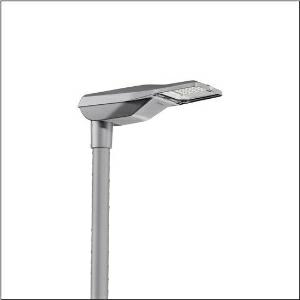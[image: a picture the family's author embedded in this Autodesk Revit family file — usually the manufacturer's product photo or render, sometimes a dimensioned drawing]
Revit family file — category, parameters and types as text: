
# Revit family: streetlight_sl_21_iq_micro___st1_5a_5xe1p31d08cb_2d79
name_source: partatom
category: Lighting Fixtures
units: mm (PartAtom-declared; Revit-internal decimal feet)

## family parameters
Cut with Voids When Loaded = No
Host = Face
Light Source = No
Part Type = Normal
Room Calculation Point = No
Round Connector Dimension = Use Diameter
Shared = No

## types (1)
- --- (1 x LED, 2820 lm, 19.4 W, 3000K)
    Apparent Load = 19 VA
    CIE Flux Codes = 22 53 95 100 100
    Color Rendering = 70
    Color Temperature = 3000K
    Default Elevation = 1800 mm
    Description = Streetlight SL 21 iQ micro, mast luminaire, primary light control with lens, of PMMA, primary optical cover: cover, of toughened safety glass, transparent, light distribution: ST1.5a, light emission: direct distribution, primary light characteristic: asymmetric, installation type: post-top, side-entry, LED, High Power LED, rated luminous flux: 2.820lm, luminous efficacy: 145lm/W, light colour: 730, colour temperature: 3000K, control gear: iQ-Comfort, control: Auto-Match, Temp-Guard, Lumen-Switch, Night-Set, Smart-Wire, Light-Fading, Desk-Remote (wireless, voltage-free reading and setting of iQ features in the workshop via application-optimized NFC function/RFID function), optimised constant luminous flux control (CLO 2.0), pre-setting: linear dimming characteristic, mains connection: 220..240V, AC, 50/60Hz, start of lifetime: 19W, end of service life: 20W, reduction: 10W, luminaire housing, of diecast aluminium, powder-coated, Siteco® metallic grey (DB 702S), corrosivity category C5 mid according to DIN EN ISO 12944, please order mast flange separately, inclination adjustable: 0°, 5°, 10°, 15°, sealing non-destructively replaceable, multi-level sealing system, length: 528mm, width: 235mm, height: 110mm, mast flange for spigot size: 42mm (side-entry): 5XC10008XM4, 60/48mm (side-entry/post-top): 5XC10108XM2, 76/60mm (side-entry/post-top): 5XC10108XM1, protection rating (complete): IP66, insulation class (complete): insulation class II (safety insulation), certification: CE, ENEC, ENEC+, VDE, impact resistance: IK10, permissible operating ambient temperature for outdoor applications: -40..+50°C, standard-compliant lighting for roads and squares, packaging unit: 1 piece

Light Distribution: ST1.5a
    Height = 110 mm
    Lamp = 1 x LED
    Lamp Light Flux = 2820 lm
    Lamp Power = 19.4 W
    Lamp count = 1
    Length = 528 mm
    Luminous efficacy = 145 lm/W
    Manufacturer = Siteco
    ModVariant = No
    Model = 5XE1P31D08CB
    Number of Poles = 1
    OnlyDefault = Yes
    Power Factor = 1
    Product Name = Streetlight SL 21 iQ micro | ST1.5a
    Product group = mast luminaire | pylon top
    ProductGroupID = 6100
    Protection Class = Protection class II
    Protection Degree = IP 66
    RLX_Detail_Level = 1
    RLX_Emergency_Light_Flux = 0 lm
    RLX_Emergency_Type = 0
    RLX_Emergency_Type_DB = No
    RlxData = <blob elided: 103009 chars, md5=6a53d1e1>
    Socket = socket
    Standby Power = 0 W
    System Light Flux = 2820 lm
    System Power = 19 W
    Type Comments = factory setting: luminous flux: 100 % | dim-lin: 254 | 387 mA
    Type Image = l_1006881.jpg
    URL = http://relux.com
    VarID = @adj_159587
    Voltage = 0 V
    Weight = 0.00 kg
    Width = 235 mm

## geometry (parser evidence)
native form markers: Blend x4, Sweep x12
no freeform markers — native parametric forms only
